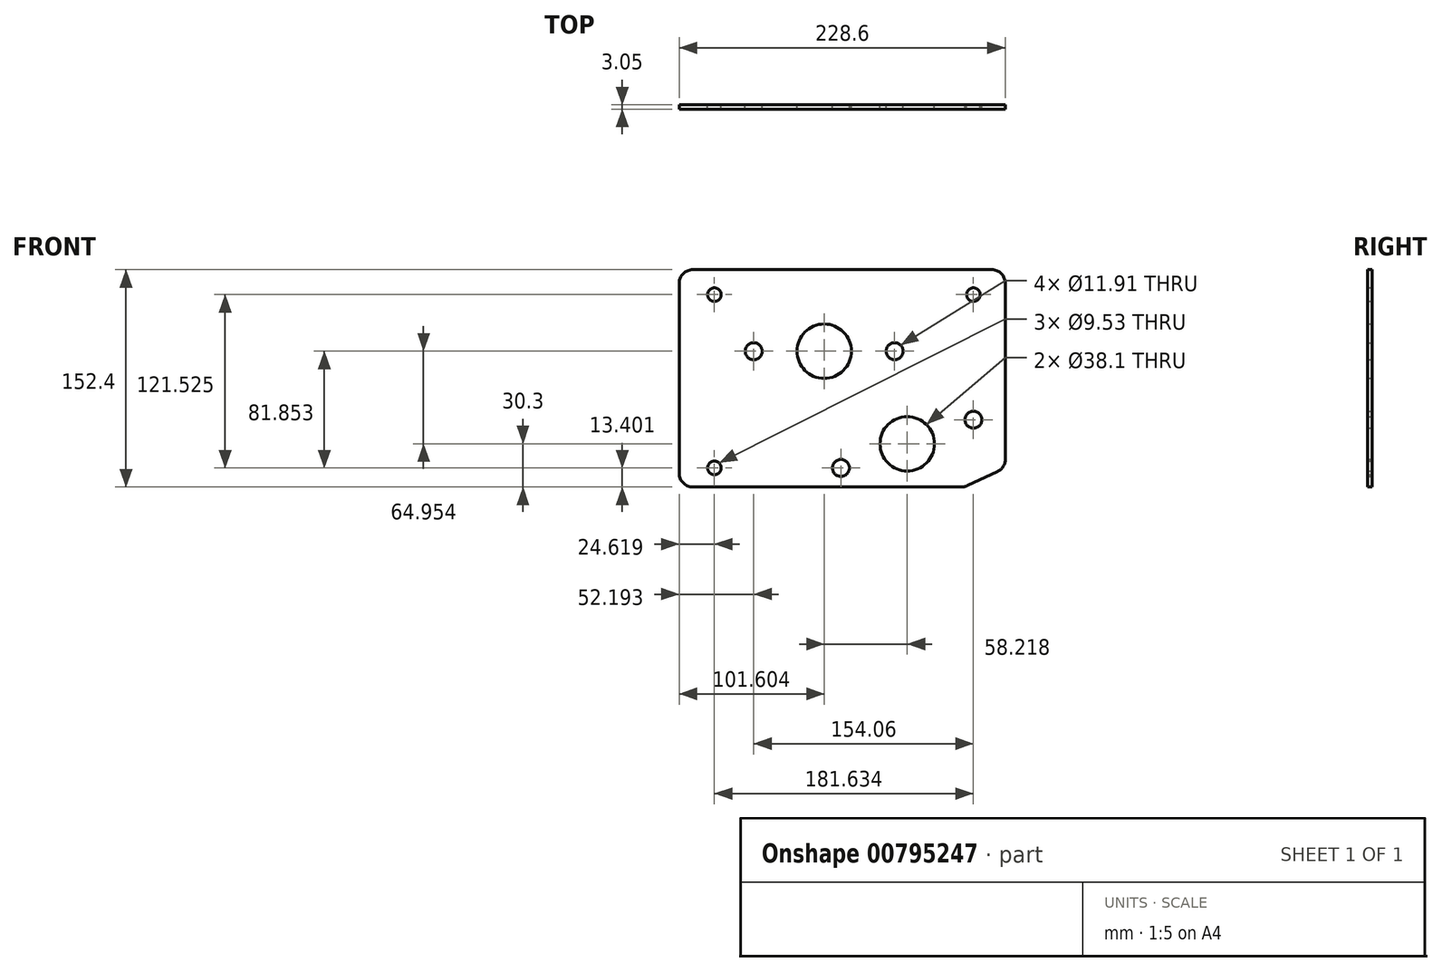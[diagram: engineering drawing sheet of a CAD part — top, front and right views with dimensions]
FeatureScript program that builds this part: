
annotation { "Feature Type Name" : "Feature", "Feature Type Description" : "" }
export const myFeature = defineFeature(function(context is Context, id is Id, definition is map)
    precondition{}
    {
        {
            var Q0;
            Q0=qCreatedBy(makeId("Front.planeOp"),FACE);
            var sketch = newSketch(context, id + "F0", { "sketchPlane" : qUnion([Q0])});
            skLineSegment(sketch, "E0", {"start": v(-189.54, 37.55) * mm, "end": v(-189.54, -95.8) * mm});
            skLineSegment(sketch, "E1", {"start": v(-180.01, -105.33) * mm, "end": v(8.38, -105.33) * mm});
            skLineSegment(sketch, "E2", {"start": v(12.4, -104.43) * mm, "end": v(33.56, -94.57) * mm});
            skLineSegment(sketch, "E3", {"start": v(39.06, -85.93) * mm, "end": v(39.06, 37.55) * mm});
            skLineSegment(sketch, "E4", {"start": v(29.54, 47.07) * mm, "end": v(-180.01, 47.07) * mm});
            skCircle(sketch, "E5", {"center": v(-87.94, -10.08) * mm, "radius": 19.05 * mm});
            skCircle(sketch, "E6", {"center": v(-29.72, -75.03) * mm, "radius": 19.05 * mm});
            skCircle(sketch, "E7", {"center": v(-76.15, -91.93) * mm, "radius": 5.95 * mm});
            skCircle(sketch, "E8", {"center": v(16.71, -58.13) * mm, "radius": 5.95 * mm});
            skCircle(sketch, "E9", {"center": v(16.71, 29.6) * mm, "radius": 4.76 * mm});
            skCircle(sketch, "E10", {"center": v(-164.92, 29.6) * mm, "radius": 4.76 * mm});
            skCircle(sketch, "E11", {"center": v(-164.92, -91.93) * mm, "radius": 4.76 * mm});
            skCircle(sketch, "E12", {"center": v(-137.35, -10.08) * mm, "radius": 5.95 * mm});
            skCircle(sketch, "E13", {"center": v(-38.52, -10.08) * mm, "radius": 5.95 * mm});
            skPoint(sketch, "E14.visualSharp", {"position": v(-189.54, 47.07) * mm});
            skArc(sketch, "E14.filletArc", {"start": v(-180.01, 47.07) * mm, "mid": v(-186.75, 44.28) * mm, "end": v(-189.54, 37.55) * mm});
            skPoint(sketch, "E15.visualSharp", {"position": v(39.06, 47.07) * mm});
            skArc(sketch, "E15.filletArc", {"start": v(39.06, 37.55) * mm, "mid": v(36.27, 44.28) * mm, "end": v(29.54, 47.07) * mm});
            skPoint(sketch, "E16.visualSharp", {"position": v(-189.54, -105.33) * mm});
            skArc(sketch, "E16.filletArc", {"start": v(-189.54, -95.8) * mm, "mid": v(-186.75, -102.54) * mm, "end": v(-180.01, -105.33) * mm});
            skPoint(sketch, "E17.visualSharp", {"position": v(39.06, -92) * mm});
            skArc(sketch, "E17.filletArc", {"start": v(33.56, -94.57) * mm, "mid": v(37.57, -91.05) * mm, "end": v(39.06, -85.93) * mm});
            skPoint(sketch, "E18.visualSharp", {"position": v(10.49, -105.33) * mm});
            skArc(sketch, "E18.filletArc", {"start": v(8.38, -105.33) * mm, "mid": v(10.44, -105.1) * mm, "end": v(12.4, -104.43) * mm});
            skSolve(sketch);
        }
        {
            var Q0;
            Q0 = qSketchRegion(id + "F0", true);
            extrude(context, id + "F1", {"entities" : qUnion([Q0]), "depth" : 3.05 * mm, "offsetDistance" : 25.4 * mm});
        }
    });
